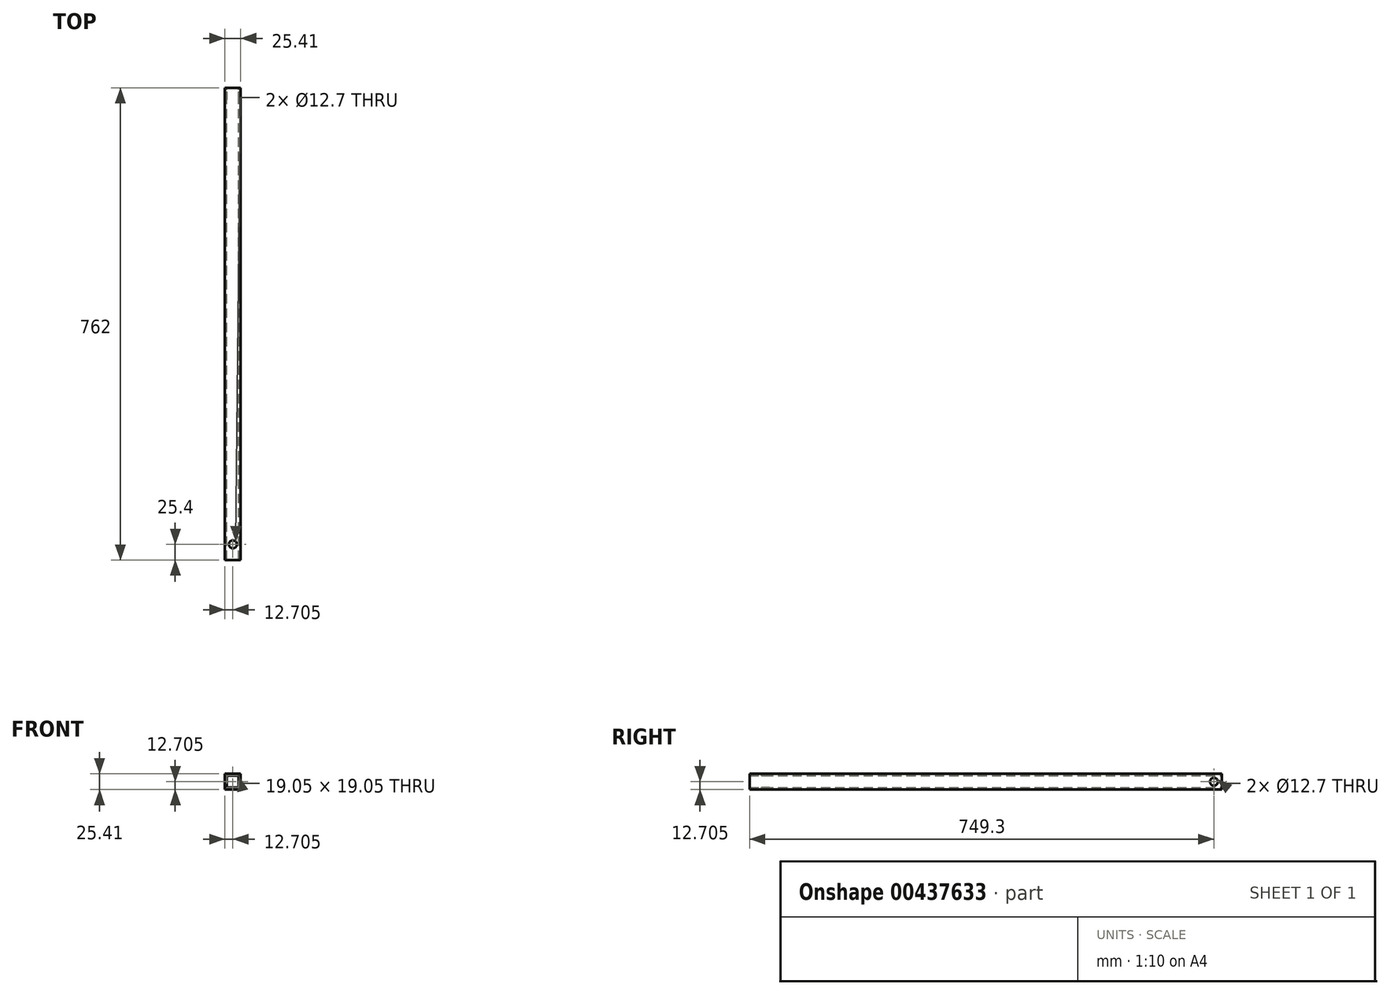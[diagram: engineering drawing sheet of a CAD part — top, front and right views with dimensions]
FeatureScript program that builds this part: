
annotation { "Feature Type Name" : "Feature", "Feature Type Description" : "" }
export const myFeature = defineFeature(function(context is Context, id is Id, definition is map)
    precondition{}
    {
        {
            var Q0;
            Q0=qCreatedBy(makeId("Front.planeOp"),FACE);
            var sketch = newSketch(context, id + "F0", { "sketchPlane" : qUnion([Q0])});
            skLineSegment(sketch, "E0.bottom", {"start": v(-22.23, 22.23) * mm, "end": v(3.17, 22.23) * mm});
            skLineSegment(sketch, "E0.top", {"start": v(-22.23, -3.18) * mm, "end": v(3.18, -3.18) * mm});
            skLineSegment(sketch, "E0.left", {"start": v(-22.23, 22.23) * mm, "end": v(-22.23, -3.18) * mm});
            skLineSegment(sketch, "E0.right", {"start": v(3.17, 22.23) * mm, "end": v(3.18, -3.18) * mm});
            skLineSegment(sketch, "E1.bottom", {"start": v(-19.05, 19.05) * mm, "end": v(0, 19.05) * mm});
            skLineSegment(sketch, "E1.top", {"start": v(-19.05, 0) * mm, "end": v(0, 0) * mm});
            skLineSegment(sketch, "E1.left", {"start": v(-19.05, 19.05) * mm, "end": v(-19.05, 0) * mm});
            skLineSegment(sketch, "E1.right", {"start": v(0, 19.05) * mm, "end": v(0, 0) * mm});
            skSolve(sketch);
        }
        {
            var Q0;
            Q0=qSketchRegion(id+"F0",true);
            extrude(context, id + "F1", {"entities" : qUnion([Q0]), "depth" : 762 * mm});
        }
        {
            var Q0;
            Q0=makeQuery(id+"F1.opExtrude","SWEPT_FACE",FACE,{"disambiguationData":[OSD([sQuery(id+"F0.wireOp",EDGE,"E0.bottom")])]});
            var sketch = newSketch(context, id + "F2", { "sketchPlane" : qUnion([Q0])});
            skLineSegment(sketch, "E2.bottom", {"start": v(-22.23, -762) * mm, "end": v(-9.53, -762) * mm});
            skLineSegment(sketch, "E2.top", {"start": v(-22.23, -736.6) * mm, "end": v(-9.53, -736.6) * mm});
            skLineSegment(sketch, "E2.left", {"start": v(-22.23, -762) * mm, "end": v(-22.23, -736.6) * mm});
            skLineSegment(sketch, "E2.right", {"start": v(-9.53, -762) * mm, "end": v(-9.53, -736.6) * mm});
            skSolve(sketch);
        }
        {
            var Q0;
            Q0=sQuery(id+"F2.wireOp",VERTEX,"E2.top.end");
            var Q1;
            Q1=makeQuery(id+"F1.opExtrude","SWEPT_BODY",BODY,{"disambiguationData":[OSD([sQuery(id+"F0.wireOp",EDGE,"E0.bottom"),sQuery(id+"F0.wireOp",EDGE,"E0.top"),sQuery(id+"F0.wireOp",EDGE,"E0.left"),sQuery(id+"F0.wireOp",EDGE,"E0.right"),sQuery(id+"F0.wireOp",EDGE,"E1.bottom"),sQuery(id+"F0.wireOp",EDGE,"E1.top"),sQuery(id+"F0.wireOp",EDGE,"E1.left"),sQuery(id+"F0.wireOp",EDGE,"E1.right")])]});
            hole(context, id + "F3", {"style" : HoleStyle.SIMPLE, "endStyle" : HoleEndStyle.THROUGH, "holeDiameter" : 12.7 * mm, "isTappedThrough" : true, "tappedDepth" : 12.7 * mm, "tapClearance" : 3, "startFromSketch" : true, "locations" : qUnion([Q0]), "scope" : qUnion([Q1])});
        }
        {
            var Q0;
            Q0=makeQuery(id+"F1.opExtrude","SWEPT_FACE",FACE,{"disambiguationData":[OSD([sQuery(id+"F0.wireOp",EDGE,"E0.right")])]});
            var sketch = newSketch(context, id + "F4", { "sketchPlane" : qUnion([Q0])});
            skLineSegment(sketch, "E3.bottom", {"start": v(0, 22.23) * mm, "end": v(-12.7, 22.23) * mm});
            skLineSegment(sketch, "E3.top", {"start": v(0, 9.52) * mm, "end": v(-12.7, 9.52) * mm});
            skLineSegment(sketch, "E3.left", {"start": v(0, 22.23) * mm, "end": v(0, 9.52) * mm});
            skLineSegment(sketch, "E3.right", {"start": v(-12.7, 22.23) * mm, "end": v(-12.7, 9.52) * mm});
            skSolve(sketch);
        }
        {
            var Q0;
            Q0=sQuery(id+"F4.wireOp",VERTEX,"E3.right.end");
            var Q1;
            Q1=makeQuery(id+"F1.opExtrude","SWEPT_BODY",BODY,{"disambiguationData":[OSD([sQuery(id+"F0.wireOp",EDGE,"E0.bottom"),sQuery(id+"F0.wireOp",EDGE,"E0.top"),sQuery(id+"F0.wireOp",EDGE,"E0.left"),sQuery(id+"F0.wireOp",EDGE,"E0.right"),sQuery(id+"F0.wireOp",EDGE,"E1.bottom"),sQuery(id+"F0.wireOp",EDGE,"E1.top"),sQuery(id+"F0.wireOp",EDGE,"E1.left"),sQuery(id+"F0.wireOp",EDGE,"E1.right")])]});
            hole(context, id + "F5", {"style" : HoleStyle.SIMPLE, "endStyle" : HoleEndStyle.THROUGH, "holeDiameter" : 12.7 * mm, "isTappedThrough" : true, "tappedDepth" : 12.7 * mm, "tapClearance" : 3, "startFromSketch" : true, "locations" : qUnion([Q0]), "scope" : qUnion([Q1])});
        }
    });
